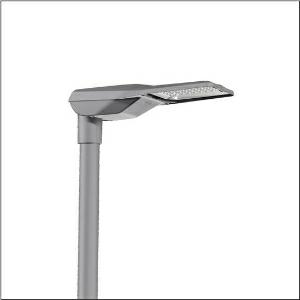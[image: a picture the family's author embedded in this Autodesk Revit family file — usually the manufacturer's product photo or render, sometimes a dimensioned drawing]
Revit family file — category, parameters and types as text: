
# Revit family: streetlight_sl_21_iq_mini___st1_0a_5xe2d41d08gb_4d7e
name_source: partatom
category: Lighting Fixtures
units: mm (PartAtom-declared; Revit-internal decimal feet)

## family parameters
Cut with Voids When Loaded = No
Host = Face
Light Source = No
Part Type = Normal
Room Calculation Point = No
Round Connector Dimension = Use Diameter
Shared = No

## types (1)
- --- (1 x LED, 5920 lm, 37.1 W, 4000K)
    Apparent Load = 37 VA
    CIE Flux Codes = 37 72 97 100 100
    Color Rendering = 70
    Color Temperature = 4000K
    Default Elevation = 1800 mm
    Description = Streetlight SL 21 iQ mini, mast luminaire, primary light control with lens, of PMMA, primary optical cover: cover, of toughened safety glass, transparent, light distribution: ST1.0a, light emission: direct distribution, primary light characteristic: asymmetric, installation type: post-top, side-entry, LED, High Power LED, rated luminous flux: 5.920lm, luminous efficacy: 160lm/W, light colour: 740, colour temperature: 4000K, control gear: iQ-Comfort, control: Auto-Match, Temp-Guard, Lumen-Switch, Night-Set, Smart-Wire, Light-Fading, Desk-Remote (wireless, voltage-free reading and setting of iQ features in the workshop via application-optimized NFC function/RFID function), optimised constant luminous flux control (CLO 2.0), pre-setting: linear dimming characteristic, mains connection: 220..240V, AC, 50/60Hz, start of lifetime: 37W, end of service life: 39W, reduction: 18W, luminaire housing, of diecast aluminium, powder-coated, Siteco® metallic grey (DB 702S), corrosivity category C5 mid according to DIN EN ISO 12944, please order mast flange separately, inclination adjustable: 0°, 5°, 10°, 15°, sealing non-destructively replaceable, multi-level sealing system, length: 628mm, width: 235mm, height: 110mm, mast flange for spigot size: 42mm (side-entry): 5XC10008XM4, 60/48mm (side-entry/post-top): 5XC10108XM2, 76/60mm (side-entry/post-top): 5XC10108XM1, mounting height: 4..8m, protection rating (complete): IP66, insulation class (complete): insulation class II (safety insulation), certification: CE, ENEC, ENEC+, VDE, impact resistance: IK10, permissible operating ambient temperature for outdoor applications: -40..+50°C, standard-compliant lighting for roads and squares, packaging unit: 1 piece

Light Distribution: ST1.0a
    Height = 110 mm
    Lamp = 1 x LED
    Lamp Light Flux = 5920 lm
    Lamp Power = 37.1 W
    Lamp count = 1
    Length = 625 mm
    Luminous efficacy = 160 lm/W
    Manufacturer = Siteco
    ModVariant = No
    Model = 5XE2D41D08GB
    Number of Poles = 1
    OnlyDefault = Yes
    Power Factor = 1
    Product Name = Streetlight SL 21 iQ mini | ST1.0a
    Product group = mast luminaire | pylon top
    ProductGroupID = 6100
    Protection Class = Protection class II
    Protection Degree = IP 66
    RLX_Detail_Level = 1
    RLX_Emergency_Light_Flux = 0 lm
    RLX_Emergency_Type = 0
    RLX_Emergency_Type_DB = No
    RlxData = <blob elided: 26325 chars, md5=bff914b9>
    Socket = socket
    Standby Power = 0 W
    System Light Flux = 5920 lm
    System Power = 37 W
    Type Comments = factory setting: luminous flux: 100 % | dim-lin: 254 | 385 mA
    Type Image = l_1003519.jpg
    URL = http://relux.com
    VarID = @adj_188878
    Voltage = 0 V
    Weight = 0.00 kg
    Width = 234 mm

## geometry (parser evidence)
native form markers: Blend x4, Sweep x10
no freeform markers — native parametric forms only
